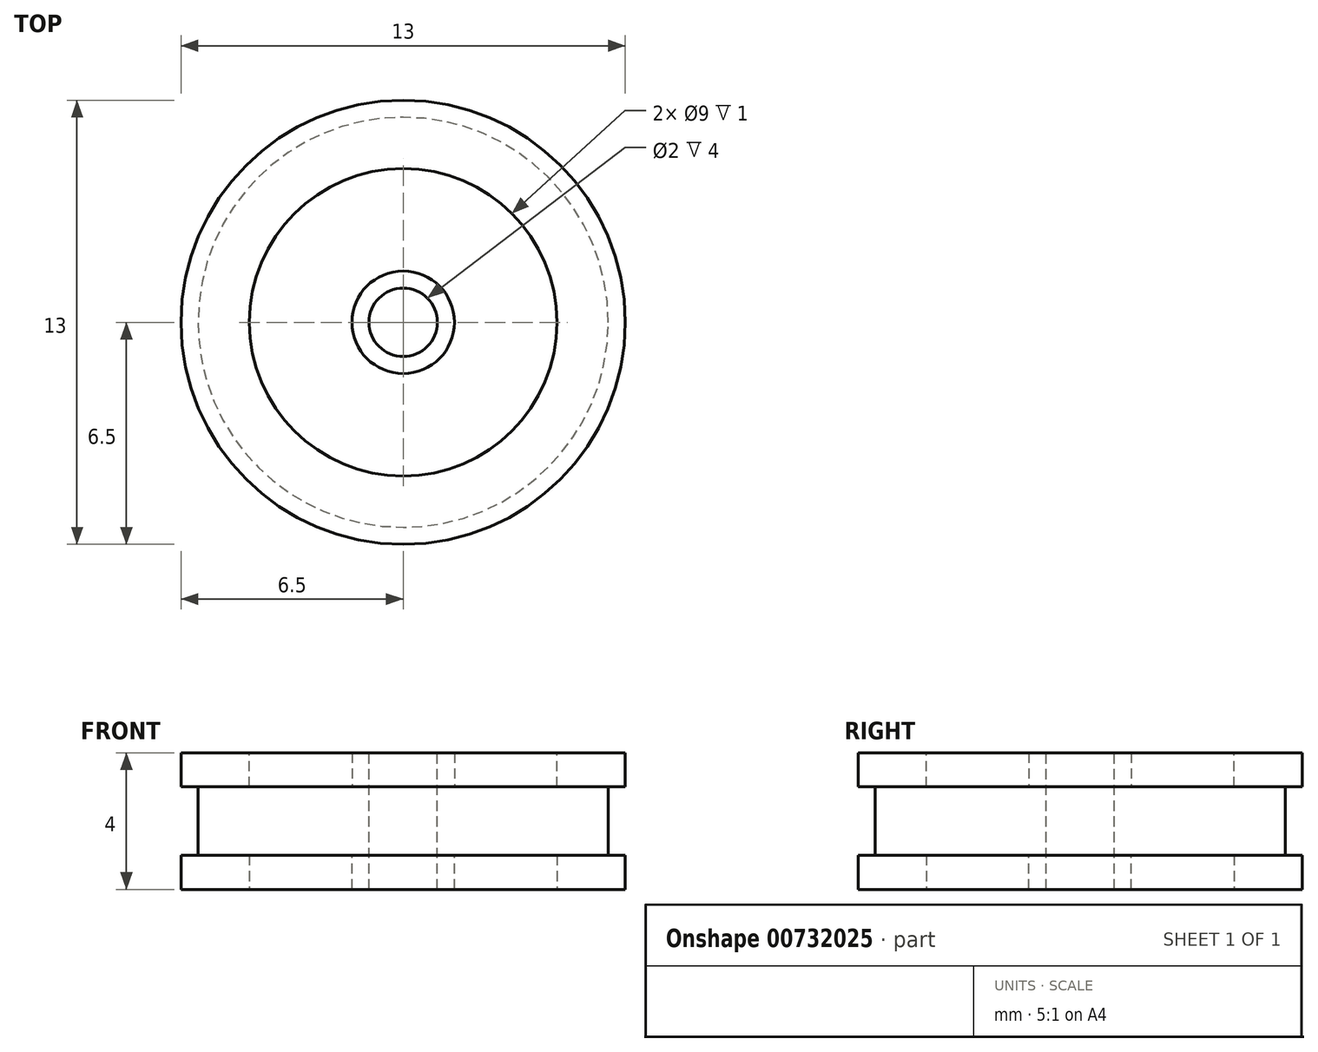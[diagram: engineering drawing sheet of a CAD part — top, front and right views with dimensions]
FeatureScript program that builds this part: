
annotation { "Feature Type Name" : "Feature", "Feature Type Description" : "" }
export const myFeature = defineFeature(function(context is Context, id is Id, definition is map)
    precondition{}
    {
        {
            var Q0;
            Q0=qCreatedBy(makeId("Top.planeOp"),FACE);
            var sketch = newSketch(context, id + "F0", { "sketchPlane" : qUnion([Q0])});
            skCircle(sketch, "E0", {"center": v(0, 0) * mm, "radius": 6.5 * mm});
            skSolve(sketch);
        }
        {
            var Q0;
            Q0 = qSketchRegion(id + "F0", true);
            extrude(context, id + "F1", {"entities" : qUnion([Q0]), "depth" : 4 * mm, "offsetDistance" : 25 * mm});
        }
        {
            var Q0;
            Q0=makeQuery(id+"F1.opExtrude","CAP_FACE",FACE,{"disambiguationData":[OSD([sQuery(id+"F0.wireOp",EDGE,"E0")])],"isStart":false});
            var sketch = newSketch(context, id + "F2", { "sketchPlane" : qUnion([Q0])});
            skCircle(sketch, "E1", {"center": v(0, 0) * mm, "radius": 4.5 * mm});
            skSolve(sketch);
        }
        {
            var Q0;
            Q0=makeQuery(id+"F2.imprint","IMPRINT",FACE,{"disambiguationData":[TD([[makeQuery(id+"F2.imprint","IMPRINT",EDGE,{"derivedFrom":sQuery(id+"F2.wireOp",EDGE,"E1")}),1.0]])]});
            extrude(context, id + "F3", {"entities" : qUnion([Q0]), "operationType" : NewBodyOperationType.REMOVE, "oppositeDirection" : true, "depth" : 1 * mm, "offsetDistance" : 25 * mm});
        }
        {
            var Q0;
            Q0=makeQuery(id+"F1.opExtrude","CAP_FACE",FACE,{"disambiguationData":[OSD([sQuery(id+"F0.wireOp",EDGE,"E0")])],"isStart":true});
            var sketch = newSketch(context, id + "F4", { "sketchPlane" : qUnion([Q0])});
            skCircle(sketch, "E2", {"center": v(0, 0) * mm, "radius": 4.5 * mm});
            skSolve(sketch);
        }
        {
            var Q0;
            Q0 = qSketchRegion(id + "F4", true);
            extrude(context, id + "F5", {"entities" : qUnion([Q0]), "operationType" : NewBodyOperationType.REMOVE, "oppositeDirection" : true, "depth" : 1 * mm, "offsetDistance" : 25 * mm});
        }
        {
            var Q0;
            Q0=makeQuery(id+"F3.boolean.opBoolean","COPY",FACE,{"derivedFrom":makeQuery(id+"F3.opExtrude","CAP_FACE",FACE,{"disambiguationData":[OSD([sQuery(id+"F2.wireOp",EDGE,"E1")])],"isStart":false})});
            var sketch = newSketch(context, id + "F6", { "sketchPlane" : qUnion([Q0])});
            skCircle(sketch, "E3", {"center": v(0, 0) * mm, "radius": 1.5 * mm});
            skSolve(sketch);
        }
        {
            var Q0;
            Q0=makeQuery(id+"F6.imprint","IMPRINT",FACE,{"disambiguationData":[TD([[makeQuery(id+"F6.imprint","IMPRINT",EDGE,{"derivedFrom":sQuery(id+"F6.wireOp",EDGE,"E3")}),1.0]])]});
            extrude(context, id + "F7", {"entities" : qUnion([Q0]), "operationType" : NewBodyOperationType.ADD, "depth" : 1 * mm, "offsetDistance" : 25 * mm});
        }
        {
            var Q0;
            Q0=makeQuery(id+"F5.boolean.opBoolean","COPY",FACE,{"derivedFrom":makeQuery(id+"F5.opExtrude","CAP_FACE",FACE,{"disambiguationData":[OSD([sQuery(id+"F4.wireOp",EDGE,"E2")])],"isStart":false})});
            var sketch = newSketch(context, id + "F8", { "sketchPlane" : qUnion([Q0])});
            skCircle(sketch, "E4", {"center": v(0, 0) * mm, "radius": 1.5 * mm});
            skSolve(sketch);
        }
        {
            var Q0;
            Q0 = qSketchRegion(id + "F8", true);
            extrude(context, id + "F9", {"entities" : qUnion([Q0]), "operationType" : NewBodyOperationType.ADD, "depth" : 1 * mm, "offsetDistance" : 25 * mm});
        }
        {
            var Q0;
            Q0=makeQuery(id+"F7.opExtrude","CAP_FACE",FACE,{"disambiguationData":[OSD([sQuery(id+"F6.wireOp",EDGE,"E3")])],"isStart":false});
            var sketch = newSketch(context, id + "F10", { "sketchPlane" : qUnion([Q0])});
            skCircle(sketch, "E5", {"center": v(0, 0) * mm, "radius": 1 * mm});
            skSolve(sketch);
        }
        {
            var Q0;
            Q0=makeQuery(id+"F10.imprint","IMPRINT",FACE,{"disambiguationData":[TD([[makeQuery(id+"F10.imprint","IMPRINT",EDGE,{"derivedFrom":sQuery(id+"F10.wireOp",EDGE,"E5")}),1.0]])]});
            extrude(context, id + "F11", {"entities" : qUnion([Q0]), "operationType" : NewBodyOperationType.REMOVE, "oppositeDirection" : true, "depth" : 25 * mm, "offsetDistance" : 25 * mm});
        }
        {
            var Q0;
            Q0=qCreatedBy(makeId("Top.planeOp"),FACE);
            cPlane(context, id + "F12", {"entities" : qUnion([Q0]), "cplaneType" : CPlaneType.OFFSET, "offset" : 1 * mm, "width" : 150 * mm, "height" : 150 * mm});
        }
        {
            var Q0;
            Q0=qCreatedBy(id+"F12.planeOp",FACE);
            var sketch = newSketch(context, id + "F13", { "sketchPlane" : qUnion([Q0])});
            skCircle(sketch, "E6", {"center": v(0, 0) * mm, "radius": 6 * mm});
            skCircle(sketch, "E7", {"center": v(0, 0) * mm, "radius": 8.66 * mm});
            skSolve(sketch);
        }
        {
            var Q0;
            Q0 = qSketchRegion(id + "F13", true);
            extrude(context, id + "F14", {"entities" : qUnion([Q0]), "operationType" : NewBodyOperationType.REMOVE, "depth" : 2 * mm, "offsetDistance" : 25 * mm});
        }
    });
